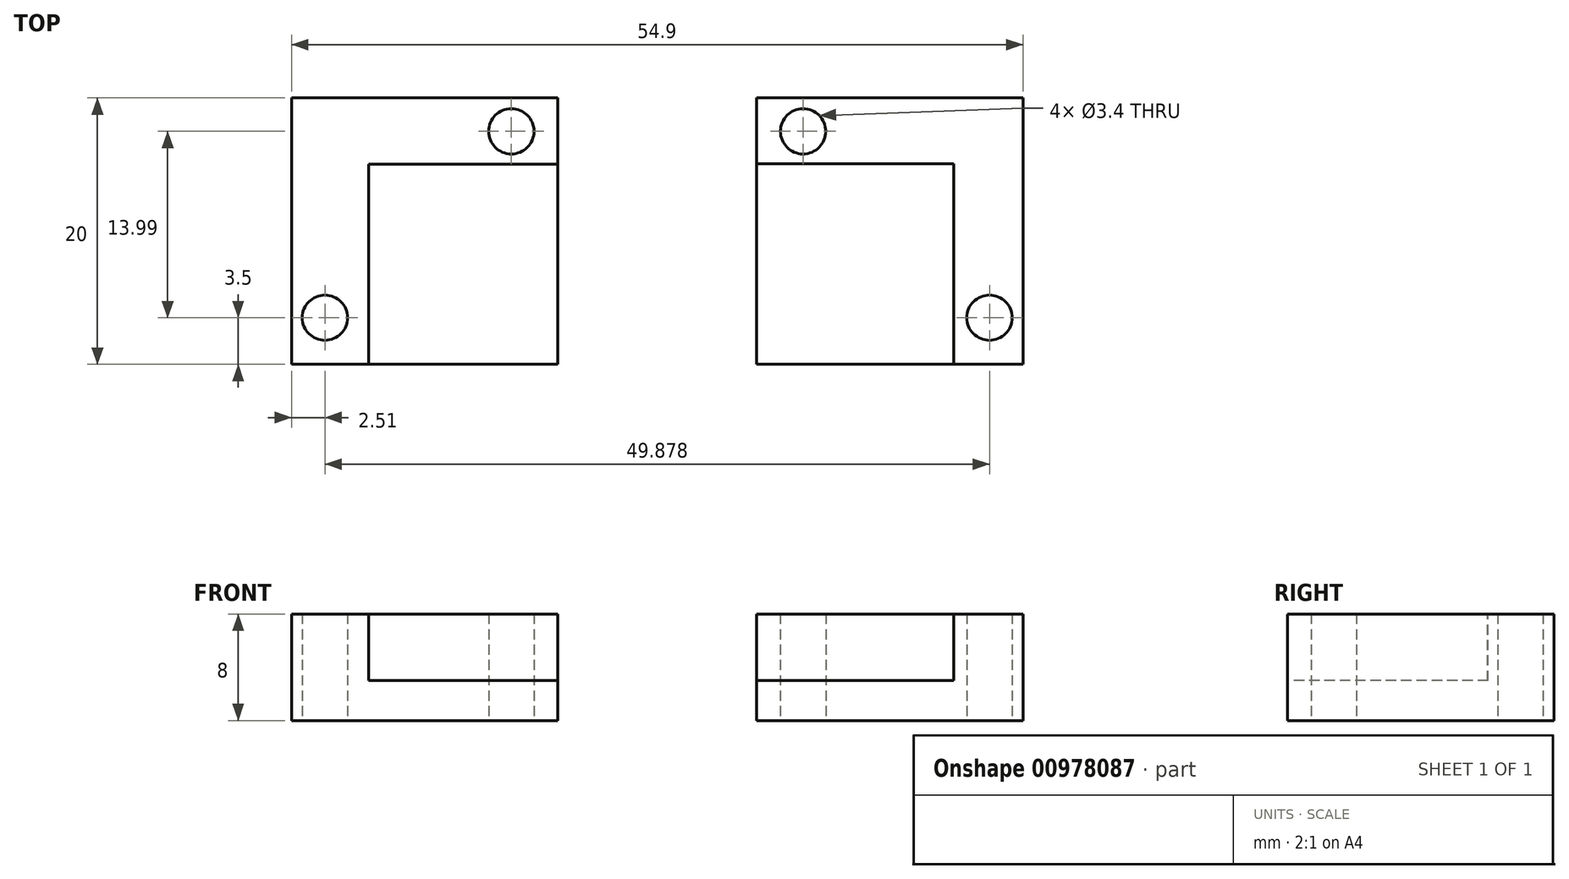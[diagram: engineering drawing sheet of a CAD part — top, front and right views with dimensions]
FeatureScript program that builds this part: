
annotation { "Feature Type Name" : "Feature", "Feature Type Description" : "" }
export const myFeature = defineFeature(function(context is Context, id is Id, definition is map)
    precondition{}
    {
        {
            var Q0;
            Q0=qCreatedBy(makeId("Top.planeOp"),FACE);
            var sketch = newSketch(context, id + "F0", { "sketchPlane" : qUnion([Q0])});
            skLineSegment(sketch, "E0.bottom", {"start": v(-10, 10) * mm, "end": v(10, 10) * mm});
            skLineSegment(sketch, "E0.top", {"start": v(-10, -10) * mm, "end": v(10, -10) * mm});
            skLineSegment(sketch, "E0.left", {"start": v(-10, 10) * mm, "end": v(-10, -10) * mm});
            skLineSegment(sketch, "E0.right", {"start": v(10, 10) * mm, "end": v(10, -10) * mm});
            skPoint(sketch, "E0.middle", {"position": v(0, 0) * mm});
            skSolve(sketch);
        }
        {
            var Q0;
            Q0=makeQuery(id+"F0.imprint","IMPRINT",FACE,{"disambiguationData":[TD([[makeQuery(id+"F0.imprint","IMPRINT",EDGE,{"derivedFrom":sQuery(id+"F0.wireOp",EDGE,"E0.bottom")}),-1.0]])]});
            extrude(context, id + "F1", {"entities" : qUnion([Q0]), "depth" : 8 * mm, "offsetDistance" : 25 * mm});
        }
        {
            var Q0;
            Q0=makeQuery(id+"F1.opExtrude","CAP_FACE",FACE,{"disambiguationData":[OSD([sQuery(id+"F0.wireOp",EDGE,"E0.bottom"),sQuery(id+"F0.wireOp",EDGE,"E0.top"),sQuery(id+"F0.wireOp",EDGE,"E0.left"),sQuery(id+"F0.wireOp",EDGE,"E0.right")])],"isStart":false});
            var sketch = newSketch(context, id + "F2", { "sketchPlane" : qUnion([Q0])});
            skLineSegment(sketch, "E1", {"start": v(-4.22, -10) * mm, "end": v(-4.22, 5.04) * mm});
            skLineSegment(sketch, "E2", {"start": v(-4.22, 5.04) * mm, "end": v(10, 5.04) * mm});
            skLineSegment(sketch, "E3", {"start": v(-4.22, -10) * mm, "end": v(10, -10) * mm});
            skLineSegment(sketch, "E4", {"start": v(10, -10) * mm, "end": v(10, 5.04) * mm});
            skSolve(sketch);
        }
        {
            var Q0;
            Q0=makeQuery(id+"F2.imprint","IMPRINT",FACE,{"disambiguationData":[TD([[makeQuery(id+"F2.imprint","IMPRINT",EDGE,{"derivedFrom":sQuery(id+"F2.wireOp",EDGE,"E1")}),-1.0]])]});
            extrude(context, id + "F3", {"entities" : qUnion([Q0]), "operationType" : NewBodyOperationType.REMOVE, "oppositeDirection" : true, "depth" : 5 * mm, "offsetDistance" : 25 * mm});
        }
        {
            var Q0;
            Q0=qCreatedBy(makeId("Top.planeOp"),FACE);
            var sketch = newSketch(context, id + "F4", { "sketchPlane" : qUnion([Q0])});
            skLineSegment(sketch, "E5.bottom", {"start": v(24.9, 10) * mm, "end": v(44.9, 10) * mm});
            skLineSegment(sketch, "E5.top", {"start": v(24.9, -10) * mm, "end": v(44.9, -10) * mm});
            skLineSegment(sketch, "E5.left", {"start": v(24.9, 10) * mm, "end": v(24.9, -10) * mm});
            skLineSegment(sketch, "E5.right", {"start": v(44.9, 10) * mm, "end": v(44.9, -10) * mm});
            skPoint(sketch, "E5.middle", {"position": v(34.9, 0) * mm});
            skSolve(sketch);
        }
        {
            var Q0;
            Q0=makeQuery(id+"F4.imprint","IMPRINT",FACE,{"disambiguationData":[TD([[makeQuery(id+"F4.imprint","IMPRINT",EDGE,{"derivedFrom":sQuery(id+"F4.wireOp",EDGE,"E5.bottom")}),-1.0]])]});
            extrude(context, id + "F5", {"entities" : qUnion([Q0]), "depth" : 8 * mm, "offsetDistance" : 25 * mm});
        }
        {
            var Q0;
            Q0=makeQuery(id+"F5.opExtrude","CAP_FACE",FACE,{"disambiguationData":[OSD([sQuery(id+"F4.wireOp",EDGE,"E5.bottom"),sQuery(id+"F4.wireOp",EDGE,"E5.top"),sQuery(id+"F4.wireOp",EDGE,"E5.left"),sQuery(id+"F4.wireOp",EDGE,"E5.right")])],"isStart":false});
            var sketch = newSketch(context, id + "F6", { "sketchPlane" : qUnion([Q0])});
            skLineSegment(sketch, "E6", {"start": v(39.7, -10) * mm, "end": v(39.7, 5.07) * mm});
            skLineSegment(sketch, "E7", {"start": v(39.7, 5.07) * mm, "end": v(24.9, 5.07) * mm});
            skLineSegment(sketch, "E8", {"start": v(24.9, 5.07) * mm, "end": v(24.9, -10) * mm});
            skLineSegment(sketch, "E9", {"start": v(24.9, -10) * mm, "end": v(39.7, -10) * mm});
            skSolve(sketch);
        }
        {
            var Q0;
            Q0=makeQuery(id+"F6.imprint","IMPRINT",FACE,{"disambiguationData":[TD([[makeQuery(id+"F6.imprint","IMPRINT",EDGE,{"derivedFrom":sQuery(id+"F6.wireOp",EDGE,"E6")}),1.0]])]});
            extrude(context, id + "F7", {"entities" : qUnion([Q0]), "operationType" : NewBodyOperationType.REMOVE, "oppositeDirection" : true, "depth" : 5 * mm, "offsetDistance" : 25 * mm});
        }
        {
            var Q0;
            Q0=qCreatedBy(makeId("Top.planeOp"),FACE);
            var sketch = newSketch(context, id + "F8", { "sketchPlane" : qUnion([Q0])});
            skCircle(sketch, "E10", {"center": v(-7.49, -6.5) * mm, "radius": 1.7 * mm});
            skCircle(sketch, "E11", {"center": v(6.5, 7.5) * mm, "radius": 1.7 * mm});
            skCircle(sketch, "E12", {"center": v(28.4, 7.49) * mm, "radius": 1.7 * mm});
            skCircle(sketch, "E13", {"center": v(42.39, -6.5) * mm, "radius": 1.7 * mm});
            skSolve(sketch);
        }
        {
            var Q0;
            Q0 = qSketchRegion(id + "F8", true);
            extrude(context, id + "F9", {"entities" : qUnion([Q0]), "operationType" : NewBodyOperationType.REMOVE, "depth" : 8.6 * mm, "offsetDistance" : 25 * mm});
        }
    });
